SOLIDWORKS PART (.sldprt)
format: sldprt  version: not decoded by parser v0  size: 98,816 bytes
history: native  units: mm
features: plane x3, sketch x3, cut_extrude x2, material x1, extrude x1 (+13 scaffold rows collapsed)
feature tree (23):
  scaffold x13  (default folders/planes/origin — collapsed)
  material  "材质 <未指定>"
  plane  "前视基准面"
  plane  "上视基准面"
  plane  "右视基准面"
  sketch  "草图2"  dims[c1.D3=~0.067805mm c1.D2=0.12mm c2.D3=~0.191026mm c2.D2=~0.206036mm c2.D1=0.1mm c3.D2=1.5mm]
  extrude  "凸台-拉伸1"  Depth=3mm
  sketch  "草图3"  dims[D3=0.2mm D4=0.2mm D1=0.725mm D2=0.725mm]
  cut_extrude  "切除-拉伸1"  Depth=3mm
  sketch  "草图4"  dims[c1.D1=1.0mm c1.D2=~0.508045mm c1.D3=0.1mm c2.D2=0.15mm]
  cut_extrude  "切除-拉伸2"  Depth=3mm
decode coverage: 6 of 6 modeling features carry decoded parameters
note: ~ marks probable driven/reference dimensions
note: suppression state not decoded; provenance and decode notes live in map.json
